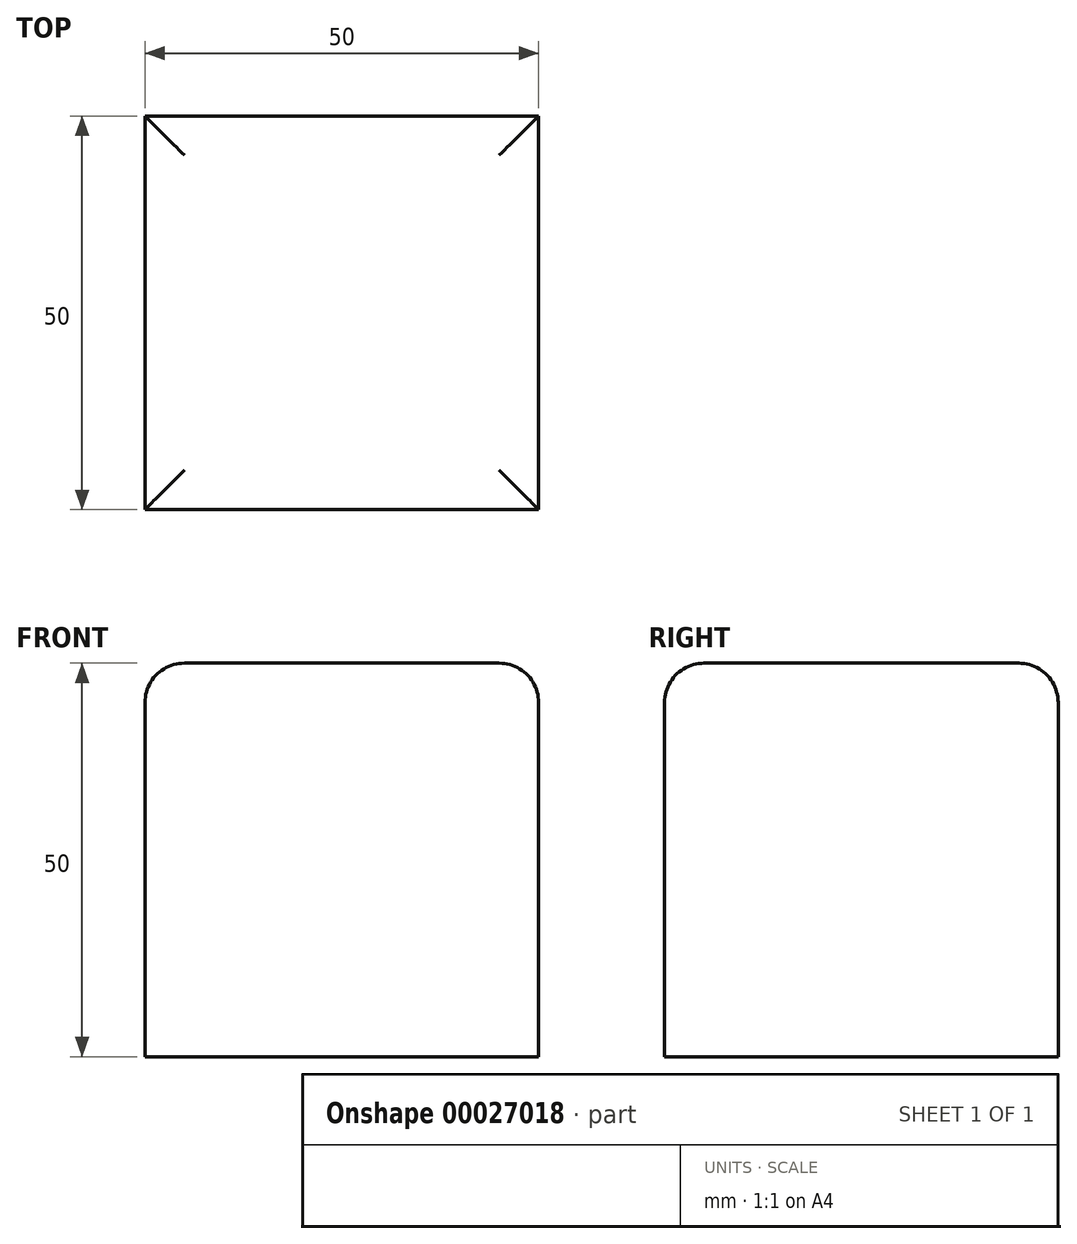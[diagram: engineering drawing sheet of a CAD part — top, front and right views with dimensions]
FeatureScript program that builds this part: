
annotation { "Feature Type Name" : "Feature", "Feature Type Description" : "" }
export const myFeature = defineFeature(function(context is Context, id is Id, definition is map)
    precondition{}
    {
        {
            var Q0;
            Q0=qCreatedBy(makeId("Top.planeOp"),FACE);
            var sketch = newSketch(context, id + "F0", { "sketchPlane" : qUnion([Q0])});
            skLineSegment(sketch, "E0.bottom", {"start": v(-19.18, 21.93) * mm, "end": v(30.82, 21.93) * mm});
            skLineSegment(sketch, "E0.top", {"start": v(-19.18, -28.07) * mm, "end": v(30.82, -28.07) * mm});
            skLineSegment(sketch, "E0.left", {"start": v(-19.18, 21.93) * mm, "end": v(-19.18, -28.07) * mm});
            skLineSegment(sketch, "E0.right", {"start": v(30.82, 21.93) * mm, "end": v(30.82, -28.07) * mm});
            skSolve(sketch);
        }
        {
            var Q0;
            Q0=makeQuery(id+"F0.imprint","IMPRINT",FACE,{"disambiguationData":[TD([[makeQuery(id+"F0.imprint","IMPRINT",EDGE,{"derivedFrom":sQuery(id+"F0.wireOp",EDGE,"E0.bottom")}),-1.0]])]});
            extrude(context, id + "F1", {"entities" : qUnion([Q0]), "depth" : 50 * mm});
        }
        {
            var Q0;
            Q0=makeQuery(id+"F1.opExtrude","CAP_EDGE",EDGE,{"disambiguationData":[OSD([sQuery(id+"F0.wireOp",EDGE,"E0.top")])],"isStart":false});
            var Q1;
            Q1=makeQuery(id+"F1.opExtrude","CAP_EDGE",EDGE,{"disambiguationData":[OSD([sQuery(id+"F0.wireOp",EDGE,"E0.right")])],"isStart":false});
            var Q2;
            Q2=makeQuery(id+"F1.opExtrude","CAP_EDGE",EDGE,{"disambiguationData":[OSD([sQuery(id+"F0.wireOp",EDGE,"E0.bottom")])],"isStart":false});
            var Q3;
            Q3=makeQuery(id+"F1.opExtrude","CAP_FACE",FACE,{"disambiguationData":[OSD([sQuery(id+"F0.wireOp",EDGE,"E0.bottom"),sQuery(id+"F0.wireOp",EDGE,"E0.top"),sQuery(id+"F0.wireOp",EDGE,"E0.left"),sQuery(id+"F0.wireOp",EDGE,"E0.right")])],"isStart":false});
            fillet(context, id + "F2", {"entities" : qUnion([Q0, Q1, Q2, Q3]), "radius" : 5 * mm, "tangentPropagation" : true, "allowEdgeOverflow" : false});
        }
    });
